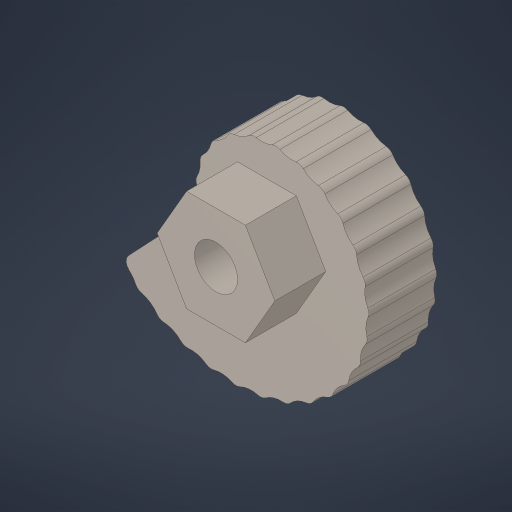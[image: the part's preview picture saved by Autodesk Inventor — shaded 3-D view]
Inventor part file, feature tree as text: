
AUTODESK INVENTOR PART (.ipt)
format: ipt  version: 2023.4 (Build 274418000, 418)  size: 274,432 bytes
history: native  units: in
note: dims shown in document units (in); Inventor stores cm internally (conversion verified against a paired STEP export)
features: fillet x1
ambient origin geometry x8: Origin, YZ Plane, XZ Plane, XY Plane, X Axis, Y Axis, Z Axis, Center Point
bodies: Solid1 (feature_tree)
feature tree (1):
  fillet  "Fillet1"  [1 undecoded]
note: 1 required parameter value undecoded (feature->parameter linkage not recoverable at this tier; creation-order binding heuristic only, values carry confidence <= 0.55)
